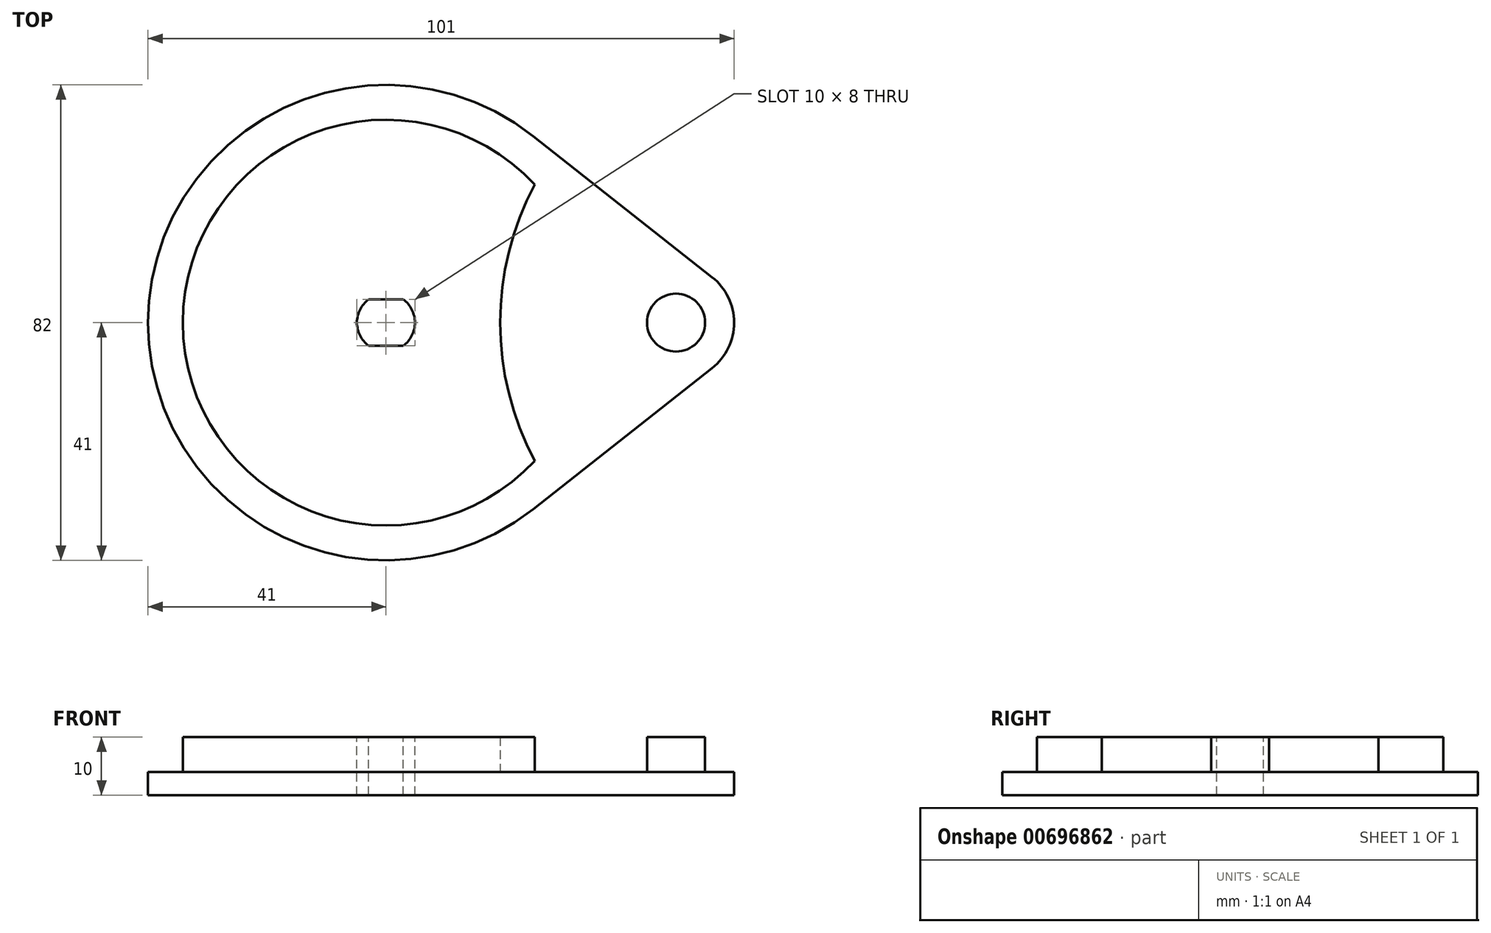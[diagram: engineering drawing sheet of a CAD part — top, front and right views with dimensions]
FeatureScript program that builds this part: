
annotation { "Feature Type Name" : "Feature", "Feature Type Description" : "" }
export const myFeature = defineFeature(function(context is Context, id is Id, definition is map)
    precondition{}
    {
        {
            var Q0;
            Q0=qCreatedBy(makeId("Top.planeOp"),FACE);
            var sketch = newSketch(context, id + "F0", { "sketchPlane" : qUnion([Q0])});
            skArc(sketch, "E0", {"start": v(25.42, 32.17) * mm, "mid": v(-41, 0) * mm, "end": v(25.42, -32.17) * mm});
            skArc(sketch, "E1", {"start": v(56.2, -7.85) * mm, "mid": v(60, 0) * mm, "end": v(56.2, 7.85) * mm});
            skLineSegment(sketch, "E2", {"start": v(25.42, 32.17) * mm, "end": v(56.2, 7.85) * mm});
            skLineSegment(sketch, "E3", {"start": v(25.42, -32.17) * mm, "end": v(56.2, -7.85) * mm});
            skSolve(sketch);
        }
        {
            var Q0;
            Q0 = qSketchRegion(id + "F0", true);
            extrude(context, id + "F1", {"entities" : qUnion([Q0]), "depth" : 4 * mm, "offsetDistance" : 25 * mm});
        }
        {
            var Q0;
            Q0=makeQuery(id+"F1.opExtrude","CAP_FACE",FACE,{"disambiguationData":[OSD([sQuery(id+"F0.wireOp",EDGE,"E0"),sQuery(id+"F0.wireOp",EDGE,"E1"),sQuery(id+"F0.wireOp",EDGE,"E2"),sQuery(id+"F0.wireOp",EDGE,"E3")])],"isStart":false});
            var sketch = newSketch(context, id + "F2", { "sketchPlane" : qUnion([Q0])});
            skArc(sketch, "E4", {"start": v(25.62, 23.85) * mm, "mid": v(-35, 0) * mm, "end": v(25.62, -23.85) * mm});
            skLineSegment(sketch, "E5", {"start": v(0, 0) * mm, "end": v(70.7, 0) * mm, "construction": true});
            skPoint(sketch, "E5.endSnap0", {"position": v(60, 0) * mm});
            skArc(sketch, "E6", {"start": v(25.62, 23.85) * mm, "mid": v(19.7, 0) * mm, "end": v(25.62, -23.85) * mm});
            skSolve(sketch);
        }
        {
            var Q0;
            Q0 = qSketchRegion(id + "F2", true);
            extrude(context, id + "F3", {"entities" : qUnion([Q0]), "operationType" : NewBodyOperationType.ADD, "depth" : 6 * mm, "offsetDistance" : 25 * mm});
        }
        {
            var Q0;
            Q0=makeQuery(id+"F1.opExtrude","CAP_FACE",FACE,{"disambiguationData":[OSD([sQuery(id+"F0.wireOp",EDGE,"E0"),sQuery(id+"F0.wireOp",EDGE,"E1"),sQuery(id+"F0.wireOp",EDGE,"E2"),sQuery(id+"F0.wireOp",EDGE,"E3")])],"isStart":false});
            var sketch = newSketch(context, id + "F4", { "sketchPlane" : qUnion([Q0])});
            skCircle(sketch, "E7", {"center": v(50, 0) * mm, "radius": 5 * mm});
            skSolve(sketch);
        }
        {
            var Q0;
            Q0 = qSketchRegion(id + "F4", true);
            extrude(context, id + "F5", {"entities" : qUnion([Q0]), "operationType" : NewBodyOperationType.ADD, "depth" : 6 * mm, "offsetDistance" : 25 * mm});
        }
        {
            var Q0;
            Q0=makeQuery(id+"F3.opExtrude","CAP_FACE",FACE,{"disambiguationData":[OSD([sQuery(id+"F2.wireOp",EDGE,"E4"),sQuery(id+"F2.wireOp",EDGE,"E6")])],"isStart":false});
            var sketch = newSketch(context, id + "F6", { "sketchPlane" : qUnion([Q0])});
            skArc(sketch, "E8", {"start": v(-3, 4) * mm, "mid": v(-5, 0) * mm, "end": v(-3, -4) * mm});
            skLineSegment(sketch, "E9", {"start": v(-3, 4) * mm, "end": v(3, 4) * mm});
            skLineSegment(sketch, "E10", {"start": v(-3, -4) * mm, "end": v(3, -4) * mm});
            skArc(sketch, "E11.trimOffspring", {"start": v(3, -4) * mm, "mid": v(5, 0) * mm, "end": v(3, 4) * mm});
            skSolve(sketch);
        }
        {
            var Q0;
            Q0 = qSketchRegion(id + "F6", true);
            extrude(context, id + "F7", {"entities" : qUnion([Q0]), "operationType" : NewBodyOperationType.REMOVE, "endBound" : BoundingType.THROUGH_ALL, "oppositeDirection" : true, "depth" : 25 * mm, "offsetDistance" : 25 * mm});
        }
    });
